# Revit family: Reece_Shower_Posh_Bristol_Shower System_Angled
name_source: partatom
category: Plumbing Fixtures
revit_build: Autodesk Revit 2018 (Build: 20190510_1515(x64)
units: mm (PartAtom-declared; Revit-internal decimal feet)

## family parameters
Cut with Voids When Loaded = Yes
Host = Face
Part Type = Normal
Room Calculation Point = Yes
Round Connector Dimension = Use Diameter
Shared = Yes

## types (1)
- 1000mm x 100mm x 2000mm_Rear Outlet
    Default Elevation = 0 mm  [stored 0 ft]
    Description = Posh Bristol Angled Shower System 1000 x 1000 x 2000mm
    Disclaimer = THIS FILE IS THE PROPERTY OF THE REECE GROUP. IT MAY NOT BE REPRODUCED, REVERSE-ENGINEERED OR MODIFIED. ANY REPUBLICATION, TRANSMISSION OR DISTRIBUTION FOR THE PURPOSE OF COMMERCIALLY EXPLOITING THE FILES IS PROHIBITED.
    Keynote = Product #2012046, Reece_Shower_Posh_Bristol_Shower System_Angled - 1000mm x 100mm x 2000mm_Rear Outlet
    Manufacturer = Posh
    Model = Bristol
    Reece_Detail_Additional = Shower System
    Reece_Detail_Disclaimer = THIS FILE IS THE PROPERTY OF THE REECE GROUP. IT MAY NOT BE REPRODUCED, REVERSE-ENGINEERED OR MODIFIED. ANY REPUBLICATION, TRANSMISSION OR DISTRIBUTION FOR THE PURPOSE OF COMMERCIALLY EXPLOITING THE FILES IS PROHIBITED.
    Reece_Detail_Function = Left or Right Hand Opening
    Reece_Material_Base = Reece_Acrylic_White
    Reece_Material_Main = Reece_Brass_Chrome
    Reece_Material_Screen = Reece_Safety Glass_Transparent
    Reece_Material_Secondary = Reece_Plastic_Transparent
    Reece_Overall_Depth = 1000 mm  [stored 3.28084 ft]
    Reece_Overall_Height = 2055 mm  [stored 6.74213 ft]
    Reece_Overall_Width = 1000 mm  [stored 3.28084 ft]
    Reece_Product_Brand = Posh
    Reece_Product_Description = Posh Bristol Angled Shower System 1000 x 1000 x 2000mm
    Reece_Product_Mount = Floor Mounted
    Reece_Product_Number = 2012046
    Reece_Product_Sub Brand = Bristol
    Reece_Product_Type = Shower
    Reece_Product_Web Page = https://www.reece.com.au
    Reece_Screen_Height = 2000 mm  [stored 6.56168 ft]
    Type Comments = Shower
    URL = https://www.reece.com.au

note: [stored X ft] marks values corroborated as IEEE doubles in the binary element streams (Revit-internal decimal feet)

## geometry (parser evidence)
native form markers: Sweep x9
no freeform markers — native parametric forms only
